# Revit family: PKSA
name_source: partatom
category: Lighting Fixtures
units: mm (PartAtom-declared; Revit-internal decimal feet)

## family parameters
Cut with Voids When Loaded = No
Host = Face
Light Source = No
OmniClass Number = 23.80.70.14
OmniClass Title = Luminaries for External Lighting
Part Type = Normal
Room Calculation Point = No
Round Connector Dimension = Use Diameter
Shared = No

## types (13) — shared parameters
Apparent Load = 0 VA
Default Elevation = 48.000"
Description = The Parkway Square® wall sconce is a beautiful addition to both interior and exterior spaces. It is available in two scales for different mounting heights and can be mounted on a wall or column.
Lamp = LED
Light Bulb Material = Glass-Frosted
Load Classification = Lighting
Manufacturer = Architectural Area Lighting
Model = Parkway Square Sconce-PKSA
Photometric Web = Web PKSA : PKSA-DB-38R111
URL = https://www.currentlighting.com
Voltage = 120 V
Wattage Comments = 24W

## per-type parameters (varying)
| type | Finish |
| PKSA- ATG | Aluminum-Antique Green |
| PKSA- AWT | Aluminum-Artic White |
| PKSA- BLK | Aluminum-Black |
| PKSA- MTB | Aluminum-Matte Black |
| PKSA- DGN | Aluminum-Dark Green |
| PKSA- DBZ | Aluminum-Dark Bronze |
| PKSA- WRZ | Aluminum-Weathered Bronze |
| PKSA- BRM | Aluminum-Metalic Bronze |
| PKSA- VBL | Aluminum-Verde Blue |
| PKSA- CRT | Aluminum-Corten |
| PKSA- MAL | Aluminum-Matte |
| PKSA- MDG | Aluminum-Medium Grey |
| PKSA- LGY | Aluminum-Light Grey |

## geometry (parser evidence)
native form markers: Blend x25, Sweep x8
no freeform markers — native parametric forms only
